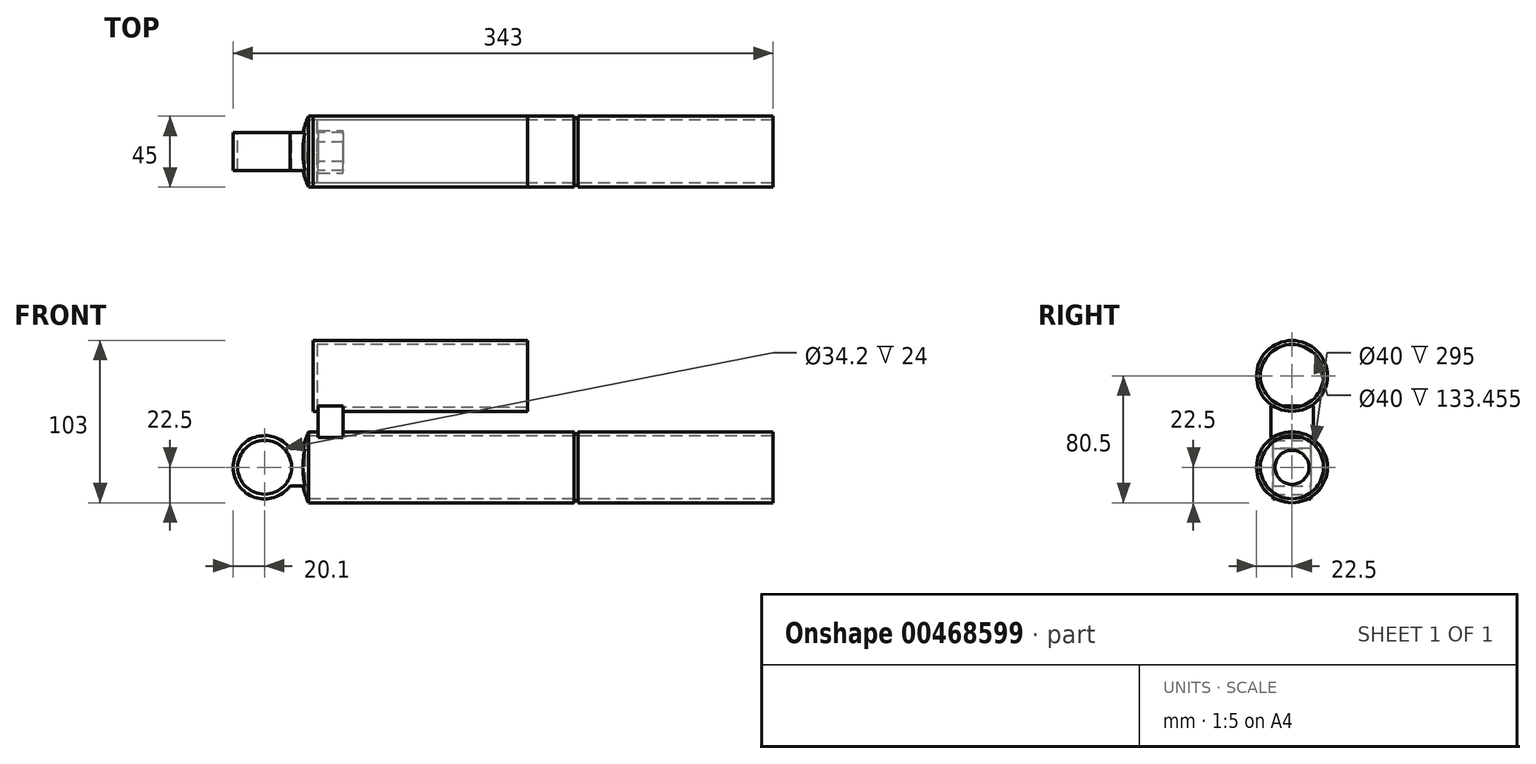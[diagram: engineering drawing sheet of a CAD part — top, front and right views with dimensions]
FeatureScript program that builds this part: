
annotation { "Feature Type Name" : "Feature", "Feature Type Description" : "" }
export const myFeature = defineFeature(function(context is Context, id is Id, definition is map)
    precondition{}
    {
        {
            var Q0;
            Q0=qCreatedBy(makeId("Front.planeOp"),FACE);
            var sketch = newSketch(context, id + "F0", { "sketchPlane" : qUnion([Q0])});
            skCircle(sketch, "E0", {"center": v(0, 0) * mm, "radius": 20.1 * mm, "construction": true});
            skCircle(sketch, "E1", {"center": v(0, 0) * mm, "radius": 17.1 * mm, "construction": true});
            skPoint(sketch, "E2", {"position": v(322.9, 0) * mm});
            skLineSegment(sketch, "E3", {"start": v(322.9, 0) * mm, "end": v(322.9, 22.5) * mm});
            skLineSegment(sketch, "E4", {"start": v(322.9, 22.5) * mm, "end": v(199.2, 22.5) * mm});
            skLineSegment(sketch, "E5", {"start": v(27.9, 22.5) * mm, "end": v(27.9, 0) * mm});
            skPoint(sketch, "E6", {"position": v(322.9, 20) * mm});
            skLineSegment(sketch, "E7", {"start": v(322.9, 20) * mm, "end": v(27.9, 20) * mm});
            skPoint(sketch, "E7.endSnap0", {"position": v(27.9, 11.25) * mm});
            skLineSegment(sketch, "E8", {"start": v(27.9, 0) * mm, "end": v(322.9, 0) * mm, "construction": true});
            skPoint(sketch, "E9", {"position": v(197.9, 22.5) * mm});
            skArc(sketch, "E10", {"start": v(196.6, 22.5) * mm, "mid": v(197.9, 21.2) * mm, "end": v(199.2, 22.5) * mm});
            skLineSegment(sketch, "E11.trimOffspring", {"start": v(196.6, 22.5) * mm, "end": v(27.9, 22.5) * mm});
            skPoint(sketch, "E12", {"position": v(22.9, 0) * mm});
            skPoint(sketch, "E13", {"position": v(27.9, -22.5) * mm});
            skArc(sketch, "E14", {"start": v(27.9, 22.5) * mm, "mid": v(24.17, 11.52) * mm, "end": v(22.9, 0) * mm});
            skPoint(sketch, "E15", {"position": v(25.4, 0) * mm});
            skPoint(sketch, "E16", {"position": v(27.9, -20) * mm});
            skArc(sketch, "E17", {"start": v(27.9, 20) * mm, "mid": v(26.03, 10.08) * mm, "end": v(25.4, 0) * mm});
            skLineSegment(sketch, "E18", {"start": v(22.9, 0) * mm, "end": v(25.4, 0) * mm});
            skSolve(sketch);
        }
        {
            var Q0;
            Q0 = qSketchRegion(id + "F0", true);
            var Q1;
            Q1=sQuery(id+"F0.wireOp",EDGE,"E8");
            revolve(context, id + "F1", {"entities" : qUnion([Q0]), "axis" : qUnion([Q1]), "revolveType" : RevolveType.FULL});
        }
        {
            var Q0;
            Q0=qCreatedBy(makeId("Front.planeOp"),FACE);
            var sketch = newSketch(context, id + "F2", { "sketchPlane" : qUnion([Q0])});
            skCircle(sketch, "E19", {"center": v(0, 0) * mm, "radius": 20.1 * mm});
            skCircle(sketch, "E20", {"center": v(0, 0) * mm, "radius": 17.1 * mm});
            skPoint(sketch, "E21", {"position": v(16.12, 12) * mm});
            skPoint(sketch, "E22", {"position": v(16.12, -12) * mm});
            skPoint(sketch, "E23", {"position": v(26.12, 12) * mm});
            skLineSegment(sketch, "E24", {"start": v(16.12, 12) * mm, "end": v(26.12, 12) * mm});
            skLineSegment(sketch, "E25", {"start": v(26.12, 12) * mm, "end": v(26.12, -12) * mm});
            skLineSegment(sketch, "E26", {"start": v(26.12, -12) * mm, "end": v(16.12, -12) * mm});
            skSolve(sketch);
        }
        {
            var Q0;
            Q0 = qSketchRegion(id + "F2", true);
            extrude(context, id + "F3", {"entities" : qUnion([Q0]), "operationType" : NewBodyOperationType.ADD, "depth" : 24 * mm, "offsetDistance" : 25 * mm, "symmetric" : true});
        }
        {
            var Q0;
            Q0=qCreatedBy(makeId("Front.planeOp"),FACE);
            var sketch = newSketch(context, id + "F4", { "sketchPlane" : qUnion([Q0])});
            skPoint(sketch, "E27", {"position": v(166.9, 58) * mm});
            skLineSegment(sketch, "E28", {"start": v(166.9, 58) * mm, "end": v(166.9, 80.5) * mm});
            skLineSegment(sketch, "E29", {"start": v(166.9, 80.5) * mm, "end": v(30.9, 80.5) * mm});
            skLineSegment(sketch, "E30", {"start": v(30.9, 80.5) * mm, "end": v(30.9, 58) * mm});
            skLineSegment(sketch, "E31", {"start": v(30.9, 58) * mm, "end": v(166.9, 58) * mm, "construction": true});
            skPoint(sketch, "E32", {"position": v(166.9, 78) * mm});
            skLineSegment(sketch, "E33", {"start": v(166.9, 78) * mm, "end": v(33.44, 78) * mm});
            skLineSegment(sketch, "E34", {"start": v(33.44, 78) * mm, "end": v(33.44, 58) * mm});
            skLineSegment(sketch, "E35", {"start": v(33.44, 58) * mm, "end": v(30.9, 58) * mm});
            skSolve(sketch);
        }
        {
            var Q0;
            Q0 = qSketchRegion(id + "F4", true);
            var Q1;
            Q1=sQuery(id+"F4.wireOp",EDGE,"E31");
            revolve(context, id + "F5", {"entities" : qUnion([Q0]), "axis" : qUnion([Q1]), "revolveType" : RevolveType.FULL});
        }
        {
            var Q0;
            Q0=qCreatedBy(makeId("Front.planeOp"),FACE);
            var sketch = newSketch(context, id + "F6", { "sketchPlane" : qUnion([Q0])});
            skPoint(sketch, "E36", {"position": v(49.9, 39) * mm});
            skLineSegment(sketch, "E37", {"start": v(49.9, 39) * mm, "end": v(49.9, 19) * mm});
            skLineSegment(sketch, "E38", {"start": v(49.9, 39) * mm, "end": v(34.1, 39) * mm});
            skLineSegment(sketch, "E39", {"start": v(34.1, 39) * mm, "end": v(34.1, 19) * mm});
            skLineSegment(sketch, "E40", {"start": v(34.1, 19) * mm, "end": v(49.9, 19) * mm});
            skPoint(sketch, "E41", {"position": v(34.1, 29) * mm});
            skSolve(sketch);
        }
        {
            var Q0;
            Q0 = qSketchRegion(id + "F6", true);
            extrude(context, id + "F7", {"entities" : qUnion([Q0]), "operationType" : NewBodyOperationType.ADD, "depth" : 27 * mm, "offsetDistance" : 25 * mm, "symmetric" : true});
        }
    });
